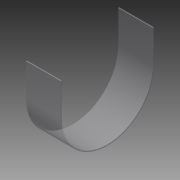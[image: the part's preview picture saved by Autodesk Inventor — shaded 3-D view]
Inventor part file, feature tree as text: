
AUTODESK INVENTOR PART (.ipt)
format: ipt  version: 2014 SP1 (Build 180222100, 222)  size: 92,672 bytes
history: native  units: in
note: dims shown in document units (in); Inventor stores cm internally (conversion verified against a paired STEP export)
features: sketch x2, extrude x1, other x1
ambient origin geometry x8: Origin, YZ Plane, XZ Plane, XY Plane, X Axis, Y Axis, Z Axis, Center Point
bodies: Solid1 (feature_tree)
feature tree (4):
  extrude  "Extrusion1"  Depth=2.0in
  other  "Bend Part1"
  sketch  "Sketch1"  dims[d0=2.0in d1=12.0in]
  sketch  "Sketch2"  dims[d2=0.0625in d3=0.0in d4=2.625in d5=180.0deg]
